# Revit family: 1776 Swoon Lounge Petit Swivel Base
name_source: partatom
category: Furniture
revit_build: Autodesk Revit 2017 (Build: 20171027_0315(x64)
units: mm (PartAtom-declared; Revit-internal decimal feet)

## family parameters
Always vertical = Yes
Cut with Voids When Loaded = No
OmniClass Number = 23.40.20.00
OmniClass Title = General Furniture and Specialties
Room Calculation Point = No
Shared = No
Work Plane-Based = No

## types (1)
- 1776 Swoon Lounge Petit Swivel Base
    Depth = 76 cm
    Description = A line extension from the Swoon Lounge, the Swoon Lounge Petit has a similar shape but it’s more upright and somewhat smaller. The one-piece shell merging the back, seat and armrests are fully upholstered and come with a seat and cushion to add even more comfort. The legs are available in solid wood. Choose from a range of fabrics and leather to customise a solution that’s ideal for hotel lobbies and suites, bar lounge areas, private homes or any corporate HQ.
    Design year = 2019
    Designer = Space Copenhagen
    Gliders = FF Plastic Black
    Height = 85 cm
    Item No. = 1776
    Legs = FF Steel Black
    Manufacturer = Fredericia Furniture
    Model = Swoon lounge Petit
    Seat Cushion = FF Sunniva 717
    Seat Height = 40 cm
    Shell = FF Sunniva 717
    Type Comments = Swoon Series
    URL = https://www.fredericia.com
    Variation Legs = Available in Chrome or Black
    Variations Upholster = Available in fabric and leather
    Weight = 18 kg
    Width = 74 cm

## geometry (parser evidence)
native form markers: Sweep x2
no freeform markers — native parametric forms only
